# Revit family: Window-Double-Hung-v1
name_source: partatom
category: Windows
units: mm (PartAtom-declared; Revit-internal decimal feet)

## family parameters
Always vertical = Yes
Cut with Voids When Loaded = No
Host = Wall
OmniClass Number = 23.30.20.17.17.14
OmniClass Title = Double-Hung Windows
Room Calculation Point = No
Shared = No

## types (7) — shared parameters
Analytic Construction = Double glazing - domestic
Assembly Code = B2020100
Construction Type Id = DG-DR
Define Thermal Properties by = Schematic Type
Fire Rating = 0.5h
Glass Panel Material = Glass
Heat Transfer Coefficient (U) = 0.5511 BTU/(h·ft²·°F)
Solar Heat Gain Coefficient = 0.76
Thermal Resistance (R) = 1.8146 (h·ft²·°F)/BTU
Top Muntin Visibility = Yes
Visual Light Transmittance = 0.81
Wall Closure = By host

## per-type parameters (varying)
| type | Bottom Muntin Visibility | Exterior Frame Material | Exterior Trim | Exterior Trim Material | Height | Interior Frame Material | Interior Trim | Interior Trim Material | Manufacturer | Muntin Height | Muntin Width | Rough Height | Rough Width | Width |
| 38" x 42" | Yes | Clad - White | Trim-Window-Exterior-Flat : with Sill | Clad - White | 3' - 6" | Wood - Stained | Trim-Window-Interior-Flat : Picture Frame | Wood - Stained |  | 1' - 5 1/8" | 2' - 8" | 3' - 6 1/2" | 3' - 2 1/2" | 3' - 2" |
| 3' x 5'7" Mullion | Yes | Black | Trim-Window-Exterior-Flat : with Sill | Black | 5' - 7 1/2" | Black | Trim-Window-Interior-Flat : Picture Frame | Black | Sierra-Pacific | 2' - 5 7/8" | 2' - 5 1/2" | 5' - 8" | 3' - 0" | 2' - 11 1/2" |
| 36 x 80 mullions | Yes | Black | Muntin Pattern_2x2 | Black | 6' - 7 1/2" | Black | Muntin Pattern_2x2 | Black | Sierra-Pacific | 2' - 11 7/8" | 2' - 5 1/2" | 6' - 8" | 3' - 0" | 2' - 11 1/2" |
| 30" x 46" | Yes | Clad - White | Trim-Window-Exterior-Flat : with Sill | Clad - White | 3' - 10" | Wood - Stained White | Trim-Window-Interior-Flat : Picture Frame | Wood - Stained White |  | 1' - 7 1/8" | 2' - 0" | 3' - 10 1/2" | 2' - 6 1/2" | 2' - 6" |
| 28" x 46" | Yes | Clad - White | Trim-Window-Exterior-Flat : with Sill | Clad - White | 3' - 10" | Wood - Stained White | Trim-Window-Interior-Flat : Picture Frame | Wood - Stained White |  | 1' - 7 1/8" | 1' - 10" | 3' - 10 1/2" | 2' - 4 1/2" | 2' - 4" |
| 36" x 67" | No | Wood - Stained White | Trim-Window-Exterior-Flat : with Sill | Wood - Stained White | 5' - 7 1/2" | Wood - Stained White | Trim-Window-Interior-Flat : Picture Frame | Wood - Stained White | Sierra-Pacific | 2' - 5 7/8" | 2' - 5 1/2" | 5' - 8" | 3' - 0" | 2' - 11 1/2" |
| 36" x 80" | No | Clad - White | Muntin Pattern_2x2 | Clad - White | 6' - 7 1/2" | Wood - Stained White | Muntin Pattern_2x2 | Wood - Stained White | Sierra-Pacific | 2' - 11 7/8" | 2' - 5 1/2" | 6' - 8" | 3' - 0" | 2' - 11 1/2" |

## geometry (parser evidence)
native form markers: Sweep x13
no freeform markers — native parametric forms only
